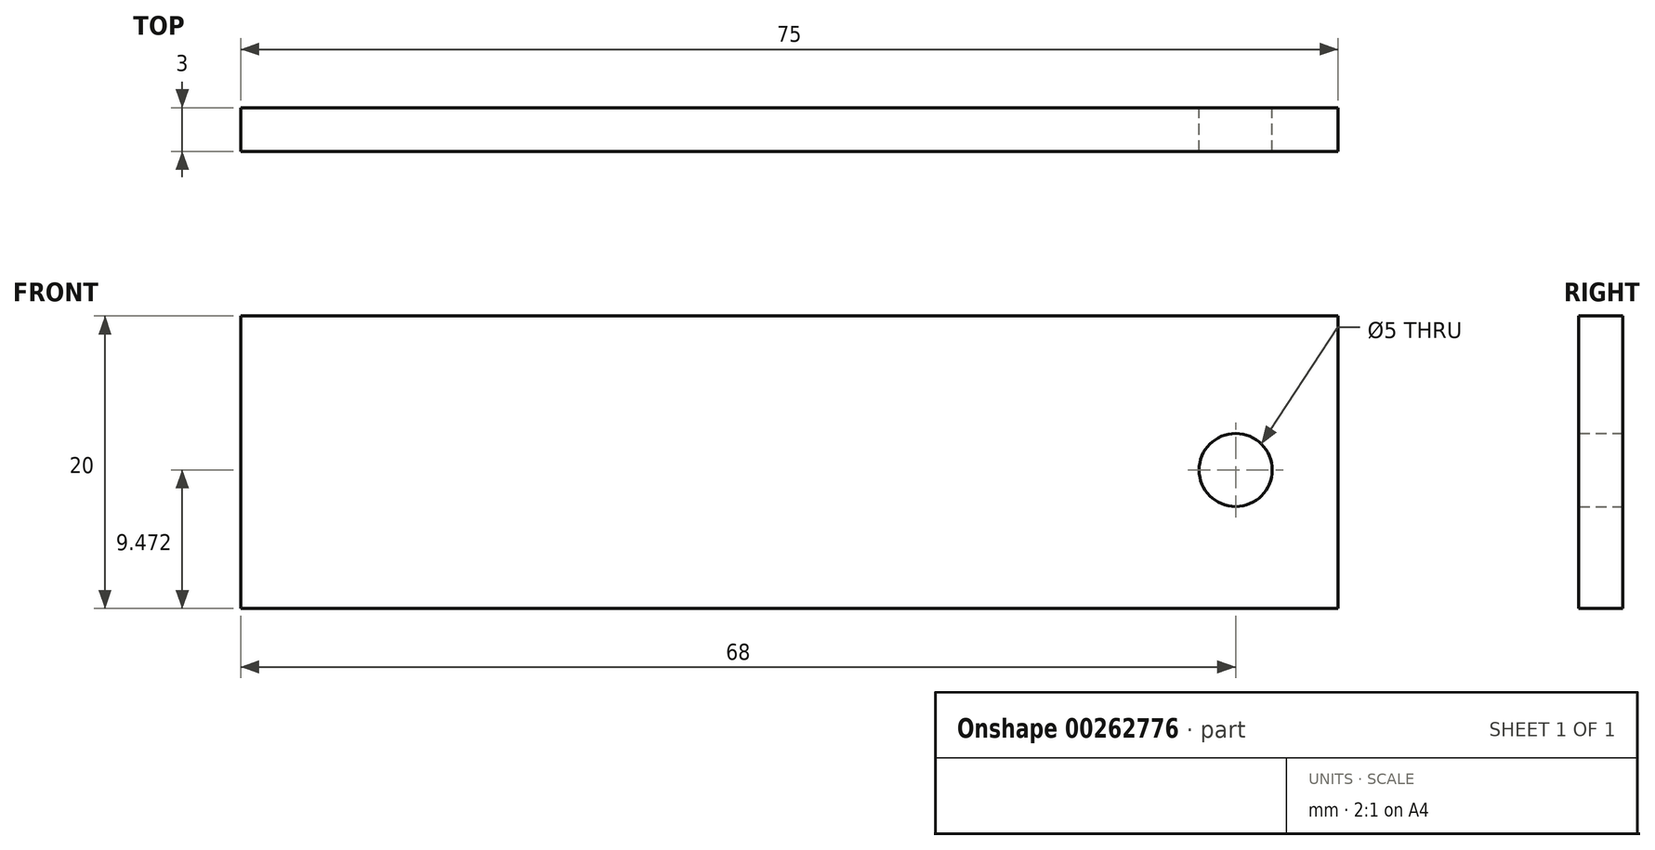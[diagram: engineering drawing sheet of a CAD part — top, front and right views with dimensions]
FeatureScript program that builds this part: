
annotation { "Feature Type Name" : "Feature", "Feature Type Description" : "" }
export const myFeature = defineFeature(function(context is Context, id is Id, definition is map)
    precondition{}
    {
        {
            var Q0;
            Q0=qCreatedBy(makeId("Front.planeOp"),FACE);
            var sketch = newSketch(context, id + "F0", { "sketchPlane" : qUnion([Q0])});
            skLineSegment(sketch, "E0.bottom", {"start": v(0, 0) * mm, "end": v(75, 0) * mm});
            skLineSegment(sketch, "E0.top", {"start": v(0, -20) * mm, "end": v(75, -20) * mm});
            skLineSegment(sketch, "E0.left", {"start": v(0, 0) * mm, "end": v(0, -20) * mm});
            skLineSegment(sketch, "E0.right", {"start": v(75, 0) * mm, "end": v(75, -20) * mm});
            skCircle(sketch, "E1", {"center": v(68, -10.53) * mm, "radius": 2.5 * mm});
            skSolve(sketch);
        }
        {
            var Q0;
            Q0=qSketchRegion(id+"F0",true);
            extrude(context, id + "F1", {"entities" : qUnion([Q0]), "depth" : 3 * mm});
        }
    });
